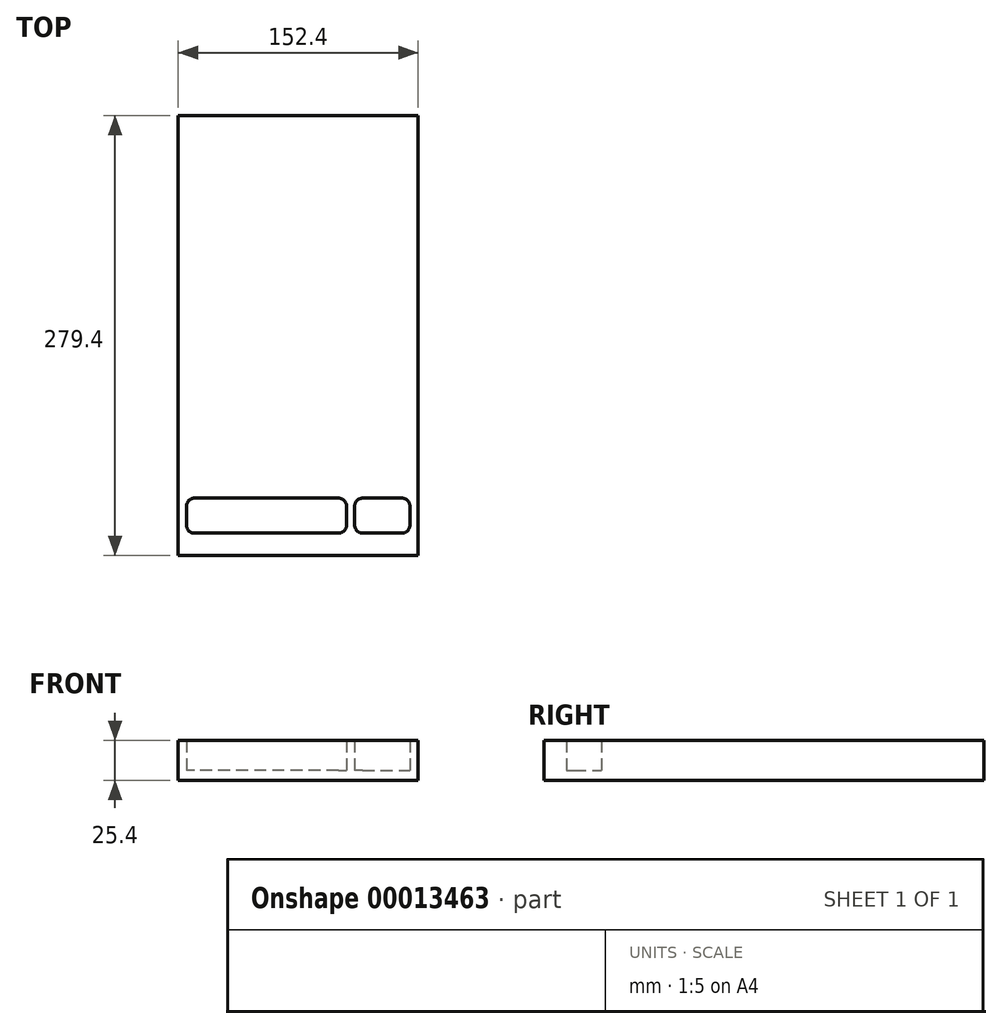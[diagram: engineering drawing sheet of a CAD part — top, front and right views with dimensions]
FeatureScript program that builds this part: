
annotation { "Feature Type Name" : "Feature", "Feature Type Description" : "" }
export const myFeature = defineFeature(function(context is Context, id is Id, definition is map)
    precondition{}
    {
        {
            var Q0;
            Q0=qCreatedBy(makeId("Top.planeOp"),FACE);
            var sketch = newSketch(context, id + "F0", { "sketchPlane" : qUnion([Q0])});
            skLineSegment(sketch, "E0.rect.bottom", {"start": v(76.2, -139.7) * mm, "end": v(-76.2, -139.7) * mm});
            skLineSegment(sketch, "E0.rect.top", {"start": v(76.2, 139.7) * mm, "end": v(-76.2, 139.7) * mm});
            skLineSegment(sketch, "E0.rect.left", {"start": v(76.2, -139.7) * mm, "end": v(76.2, 139.7) * mm});
            skLineSegment(sketch, "E0.rect.right", {"start": v(-76.2, -139.7) * mm, "end": v(-76.2, 139.7) * mm});
            skPoint(sketch, "E0.rect.middle", {"position": v(0, 0) * mm});
            skLineSegment(sketch, "E1", {"start": v(-76.2, 0) * mm, "end": v(76.2, 0) * mm, "construction": true});
            skLineSegment(sketch, "E2", {"start": v(0, 0) * mm, "end": v(0, -139.7) * mm, "construction": true});
            skLineSegment(sketch, "E3", {"start": v(-76.2, -88.9) * mm, "end": v(0, -88.9) * mm, "construction": true});
            skLineSegment(sketch, "E4", {"start": v(0, -88.9) * mm, "end": v(0, -139.7) * mm, "construction": true});
            skLineSegment(sketch, "E5.rect.bottom", {"start": v(30.67, -125.57) * mm, "end": v(-70.93, -125.57) * mm});
            skLineSegment(sketch, "E5.rect.top", {"start": v(30.67, -103.34) * mm, "end": v(-70.93, -103.34) * mm});
            skLineSegment(sketch, "E5.rect.left", {"start": v(30.67, -125.57) * mm, "end": v(30.67, -103.34) * mm});
            skLineSegment(sketch, "E5.rect.right", {"start": v(-70.93, -125.57) * mm, "end": v(-70.93, -103.34) * mm});
            skPoint(sketch, "E5.rect.middle", {"position": v(-70.93, -114.45) * mm});
            skLineSegment(sketch, "E6.bottom", {"start": v(35.93, -103.34) * mm, "end": v(70.93, -103.34) * mm});
            skLineSegment(sketch, "E6.top", {"start": v(35.93, -125.57) * mm, "end": v(70.93, -125.57) * mm});
            skLineSegment(sketch, "E6.left", {"start": v(35.93, -103.34) * mm, "end": v(35.93, -125.57) * mm});
            skLineSegment(sketch, "E6.right", {"start": v(70.93, -103.34) * mm, "end": v(70.93, -125.57) * mm});
            skLineSegment(sketch, "E7", {"start": v(-70.93, -103.34) * mm, "end": v(-76.2, -103.34) * mm, "construction": true});
            skLineSegment(sketch, "E8", {"start": v(30.67, -103.34) * mm, "end": v(35.93, -103.34) * mm, "construction": true});
            skLineSegment(sketch, "E9", {"start": v(70.93, -103.34) * mm, "end": v(76.2, -103.34) * mm, "construction": true});
            skSolve(sketch);
        }
        {
            var Q0;
            Q0 = qSketchRegion(id + "F0", true);
            extrude(context, id + "F1", {"entities" : qUnion([Q0]), "depth" : 25.4 * mm});
        }
        {
            var Q0;
            Q0=makeQuery(id+"F0.imprint","IMPRINT",FACE,{"disambiguationData":[TD([[makeQuery(id+"F0.imprint","IMPRINT",EDGE,{"derivedFrom":sQuery(id+"F0.wireOp",EDGE,"E5.rect.bottom")}),-1.0]])]});
            var Q1;
            Q1=makeQuery(id+"F0.imprint","IMPRINT",FACE,{"disambiguationData":[TD([[makeQuery(id+"F0.imprint","IMPRINT",EDGE,{"derivedFrom":sQuery(id+"F0.wireOp",EDGE,"E6.bottom")}),-1.0]])]});
            extrude(context, id + "F2", {"entities" : qUnion([Q0, Q1]), "operationType" : NewBodyOperationType.ADD, "depth" : 6.35 * mm});
        }
        {
            var Q0;
            Q0=makeQuery(id+"F1.opExtrude","SWEPT_EDGE",EDGE,{"disambiguationData":[OSD([sQuery(id+"F0.wireOp",EDGE,"E5.rect.top"),sQuery(id+"F0.wireOp",EDGE,"E5.rect.right")])]});
            var Q1;
            Q1=makeQuery(id+"F1.opExtrude","SWEPT_EDGE",EDGE,{"disambiguationData":[OSD([sQuery(id+"F0.wireOp",EDGE,"E5.rect.bottom"),sQuery(id+"F0.wireOp",EDGE,"E5.rect.right")])]});
            var Q2;
            Q2=makeQuery(id+"F1.opExtrude","SWEPT_EDGE",EDGE,{"disambiguationData":[OSD([sQuery(id+"F0.wireOp",EDGE,"E5.rect.top"),sQuery(id+"F0.wireOp",EDGE,"E5.rect.left")])]});
            var Q3;
            Q3=makeQuery(id+"F1.opExtrude","SWEPT_EDGE",EDGE,{"disambiguationData":[OSD([sQuery(id+"F0.wireOp",EDGE,"E5.rect.bottom"),sQuery(id+"F0.wireOp",EDGE,"E5.rect.left")])]});
            var Q4;
            Q4=makeQuery(id+"F1.opExtrude","SWEPT_EDGE",EDGE,{"disambiguationData":[OSD([sQuery(id+"F0.wireOp",EDGE,"E6.bottom"),sQuery(id+"F0.wireOp",EDGE,"E6.right")])]});
            var Q5;
            Q5=makeQuery(id+"F1.opExtrude","SWEPT_EDGE",EDGE,{"disambiguationData":[OSD([sQuery(id+"F0.wireOp",EDGE,"E6.bottom"),sQuery(id+"F0.wireOp",EDGE,"E6.left")])]});
            var Q6;
            Q6=makeQuery(id+"F1.opExtrude","SWEPT_EDGE",EDGE,{"disambiguationData":[OSD([sQuery(id+"F0.wireOp",EDGE,"E6.top"),sQuery(id+"F0.wireOp",EDGE,"E6.left")])]});
            var Q7;
            Q7=makeQuery(id+"F1.opExtrude","SWEPT_EDGE",EDGE,{"disambiguationData":[OSD([sQuery(id+"F0.wireOp",EDGE,"E6.top"),sQuery(id+"F0.wireOp",EDGE,"E6.right")])]});
            var Q8;
            Q8=makeQuery(id+"F2.opExtrude","CAP_EDGE",EDGE,{"disambiguationData":[OSD([sQuery(id+"F0.wireOp",EDGE,"E6.bottom")])],"isStart":false});
            var Q9;
            Q9=makeQuery(id+"F2.opExtrude","CAP_EDGE",EDGE,{"disambiguationData":[OSD([sQuery(id+"F0.wireOp",EDGE,"E6.top")])],"isStart":false});
            fillet(context, id + "F3", {"entities" : qUnion([Q0, Q1, Q2, Q3, Q4, Q5, Q6, Q7, Q8, Q9]), "radius" : 5 * mm, "tangentPropagation" : true, "allowEdgeOverflow" : false});
        }
    });
